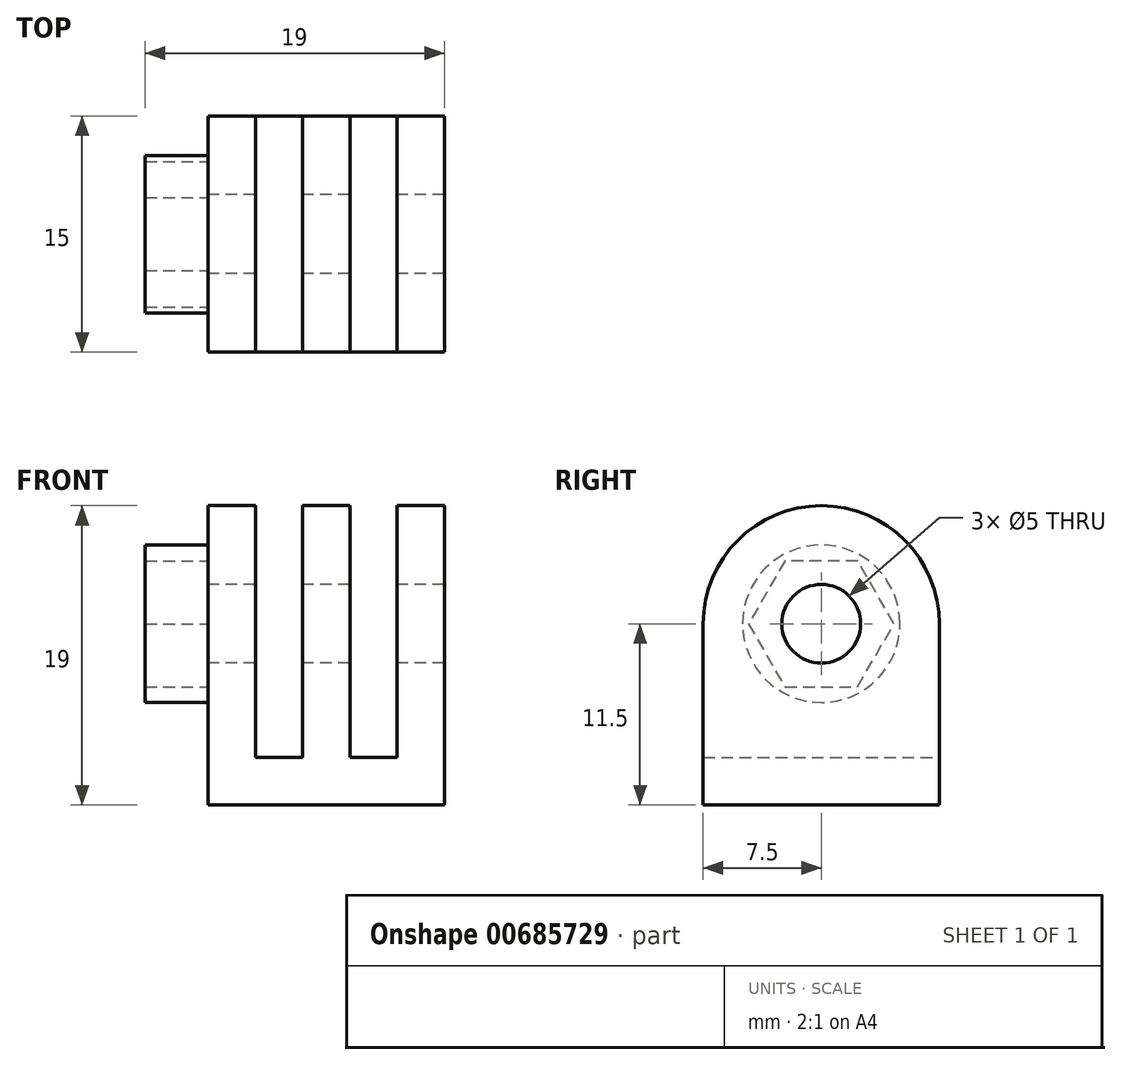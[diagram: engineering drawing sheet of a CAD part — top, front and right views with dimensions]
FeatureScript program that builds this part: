
annotation { "Feature Type Name" : "Feature", "Feature Type Description" : "" }
export const myFeature = defineFeature(function(context is Context, id is Id, definition is map)
    precondition{}
    {
        {
            assignVariable(context, id + "F0", {"name" : "BoltDiameter", "anyValue" : 5 * mm});
        }
        {
            assignVariable(context, id + "F1", {"name" : "JointDiam", "anyValue" : 15 * mm});
        }
        {
            var Q0;
            Q0=qCreatedBy(makeId("Top.planeOp"),FACE);
            var sketch = newSketch(context, id + "F2", { "sketchPlane" : qUnion([Q0])});
            skLineSegment(sketch, "E0.bottom", {"start": v(7.5, 7.5) * mm, "end": v(-7.5, 7.5) * mm});
            skLineSegment(sketch, "E0.top", {"start": v(7.5, -7.5) * mm, "end": v(-7.5, -7.5) * mm});
            skLineSegment(sketch, "E0.left", {"start": v(7.5, 7.5) * mm, "end": v(7.5, -7.5) * mm});
            skLineSegment(sketch, "E0.right", {"start": v(-7.5, 7.5) * mm, "end": v(-7.5, -7.5) * mm});
            skPoint(sketch, "E0.middle", {"position": v(0, 0) * mm});
            skSolve(sketch);
        }
        {
            var Q0;
            Q0=makeQuery(id+"F2.imprint","IMPRINT",FACE,{"disambiguationData":[TD([[makeQuery(id+"F2.imprint","IMPRINT",EDGE,{"derivedFrom":sQuery(id+"F2.wireOp",EDGE,"E0.bottom")}),1.0]])]});
            extrude(context, id + "F3", {"entities" : qUnion([Q0]), "oppositeDirection" : true, "depth" : 3 * mm, "offsetDistance" : 25 * mm});
        }
        {
            var Q0;
            Q0=makeQuery(id+"F3.opExtrude","CAP_FACE",FACE,{"disambiguationData":[OSD([sQuery(id+"F2.wireOp",EDGE,"E0.bottom"),sQuery(id+"F2.wireOp",EDGE,"E0.top"),sQuery(id+"F2.wireOp",EDGE,"E0.left"),sQuery(id+"F2.wireOp",EDGE,"E0.right")])],"isStart":true});
            var sketch = newSketch(context, id + "F4", { "sketchPlane" : qUnion([Q0])});
            skLineSegment(sketch, "E1.bottom", {"start": v(-7.5, -7.5) * mm, "end": v(-4.5, -7.5) * mm});
            skLineSegment(sketch, "E1.top", {"start": v(-7.5, 7.5) * mm, "end": v(-4.5, 7.5) * mm});
            skLineSegment(sketch, "E1.left", {"start": v(-7.5, -7.5) * mm, "end": v(-7.5, 7.5) * mm});
            skLineSegment(sketch, "E1.right", {"start": v(-4.5, -7.5) * mm, "end": v(-4.5, 7.5) * mm});
            skLineSegment(sketch, "E2.1.0.0", {"start": v(1.5, -7.5) * mm, "end": v(1.5, 7.5) * mm});
            skLineSegment(sketch, "E2.1.0.1", {"start": v(-1.5, -7.5) * mm, "end": v(-1.5, 7.5) * mm});
            skLineSegment(sketch, "E2.1.0.2", {"start": v(-1.5, -7.5) * mm, "end": v(1.5, -7.5) * mm});
            skLineSegment(sketch, "E2.1.0.3", {"start": v(-1.5, 7.5) * mm, "end": v(1.5, 7.5) * mm});
            skLineSegment(sketch, "E2.2.0.0", {"start": v(7.5, -7.5) * mm, "end": v(7.5, 7.5) * mm});
            skLineSegment(sketch, "E2.2.0.1", {"start": v(4.5, -7.5) * mm, "end": v(4.5, 7.5) * mm});
            skLineSegment(sketch, "E2.2.0.2", {"start": v(4.5, -7.5) * mm, "end": v(7.5, -7.5) * mm});
            skLineSegment(sketch, "E2.2.0.3", {"start": v(4.5, 7.5) * mm, "end": v(7.5, 7.5) * mm});
            skLineSegment(sketch, "E2.direction1", {"start": v(-7.5, -7.5) * mm, "end": v(-1.5, -7.5) * mm, "construction": true});
            skSolve(sketch);
        }
        {
            var Q0;
            Q0=makeQuery(id+"F4.imprint","IMPRINT",FACE,{"disambiguationData":[TD([[makeQuery(id+"F4.imprint","IMPRINT",EDGE,{"derivedFrom":sQuery(id+"F4.wireOp",EDGE,"E1.bottom")}),-1.0]])]});
            var Q1;
            Q1=makeQuery(id+"F4.imprint","IMPRINT",FACE,{"disambiguationData":[TD([[makeQuery(id+"F4.imprint","IMPRINT",EDGE,{"derivedFrom":sQuery(id+"F4.wireOp",EDGE,"E2.1.0.0")}),1.0]])]});
            var Q2;
            Q2=makeQuery(id+"F4.imprint","IMPRINT",FACE,{"disambiguationData":[TD([[makeQuery(id+"F4.imprint","IMPRINT",EDGE,{"derivedFrom":sQuery(id+"F4.wireOp",EDGE,"E2.2.0.0")}),-1.0]])]});
            extrude(context, id + "F5", {"entities" : qUnion([Q0, Q1, Q2]), "operationType" : NewBodyOperationType.ADD, "depth" : getVariable(context, 'JointDiam') + 1 * mm, "offsetDistance" : 25 * mm});
        }
        {
            var Q0;
            Q0=makeQuery(id+"F5.opExtrude","CAP_EDGE",EDGE,{"disambiguationData":[OSD([sQuery(id+"F4.wireOp",EDGE,"E1.top")])],"isStart":false});
            var Q1;
            Q1=makeQuery(id+"F5.opExtrude","CAP_EDGE",EDGE,{"disambiguationData":[OSD([sQuery(id+"F4.wireOp",EDGE,"E2.1.0.3")])],"isStart":false});
            var Q2;
            Q2=makeQuery(id+"F5.opExtrude","CAP_EDGE",EDGE,{"disambiguationData":[OSD([sQuery(id+"F4.wireOp",EDGE,"E2.2.0.3")])],"isStart":false});
            var Q3;
            Q3=makeQuery(id+"F5.opExtrude","CAP_EDGE",EDGE,{"disambiguationData":[OSD([sQuery(id+"F4.wireOp",EDGE,"E1.bottom")])],"isStart":false});
            var Q4;
            Q4=makeQuery(id+"F5.opExtrude","CAP_EDGE",EDGE,{"disambiguationData":[OSD([sQuery(id+"F4.wireOp",EDGE,"E2.1.0.2")])],"isStart":false});
            var Q5;
            Q5=makeQuery(id+"F5.opExtrude","CAP_EDGE",EDGE,{"disambiguationData":[OSD([sQuery(id+"F4.wireOp",EDGE,"E2.2.0.2")])],"isStart":false});
            fillet(context, id + "F6", {"entities" : qUnion([Q0, Q1, Q2, Q3, Q4, Q5]), "radius" : getVariable(context, 'JointDiam') / 2, "tangentPropagation" : true, "allowEdgeOverflow" : false});
        }
        {
            var Q0;
            Q0=makeQuery(id+"F5.boolean.opBoolean","MERGE",FACE,{"derivedFrom":[makeQuery(id+"F3.opExtrude","SWEPT_FACE",FACE,{"disambiguationData":[OSD([sQuery(id+"F2.wireOp",EDGE,"E0.right")])]}),makeQuery(id+"F5.opExtrude","SWEPT_FACE",FACE,{"disambiguationData":[OSD([sQuery(id+"F4.wireOp",EDGE,"E1.left")])]})]});
            var sketch = newSketch(context, id + "F7", { "sketchPlane" : qUnion([Q0])});
            skPoint(sketch, "E3", {"position": v(0, 8.5) * mm});
            skCircle(sketch, "E4", {"center": v(0, 8.5) * mm, "radius": 5 * mm});
            skCircle(sketch, "E5.cCircle", {"center": v(0, 8.5) * mm, "radius": 4 * mm, "construction": true});
            skLineSegment(sketch, "E5.0", {"start": v(-2.3, 12.5) * mm, "end": v(2.3, 12.5) * mm});
            skLineSegment(sketch, "E5.1", {"start": v(2.3, 12.5) * mm, "end": v(4.62, 8.5) * mm});
            skLineSegment(sketch, "E5.2", {"start": v(4.62, 8.5) * mm, "end": v(2.3, 4.5) * mm});
            skLineSegment(sketch, "E5.3", {"start": v(2.3, 4.5) * mm, "end": v(-2.3, 4.5) * mm});
            skLineSegment(sketch, "E5.4", {"start": v(-2.3, 4.5) * mm, "end": v(-4.62, 8.5) * mm});
            skLineSegment(sketch, "E5.5", {"start": v(-4.62, 8.5) * mm, "end": v(-2.3, 12.5) * mm});
            skPoint(sketch, "E5.0.midPoint", {"position": v(0, 12.5) * mm});
            skSolve(sketch);
        }
        {
            var Q0;
            Q0=sQuery(id+"F7.wireOp",VERTEX,"E3");
            var Q1;
            Q1=makeQuery(id+"F3.opExtrude","SWEPT_BODY",BODY,{"disambiguationData":[OSD([sQuery(id+"F2.wireOp",EDGE,"E0.bottom"),sQuery(id+"F2.wireOp",EDGE,"E0.top"),sQuery(id+"F2.wireOp",EDGE,"E0.left"),sQuery(id+"F2.wireOp",EDGE,"E0.right")])]});
            hole(context, id + "F8", {"style" : HoleStyle.SIMPLE, "endStyle" : HoleEndStyle.THROUGH, "holeDiameter" : getVariable(context, 'BoltDiameter'), "majorDiameter" : 5 * mm, "isTappedThrough" : true, "tappedDepth" : 12 * mm, "tapClearance" : 3, "locations" : qUnion([Q0]), "scope" : qUnion([Q1])});
        }
        {
            var Q0;
            Q0 = qSketchRegion(id + "F7", true);
            extrude(context, id + "F9", {"entities" : qUnion([Q0]), "operationType" : NewBodyOperationType.ADD, "depth" : 4 * mm, "offsetDistance" : 25 * mm});
        }
    });
